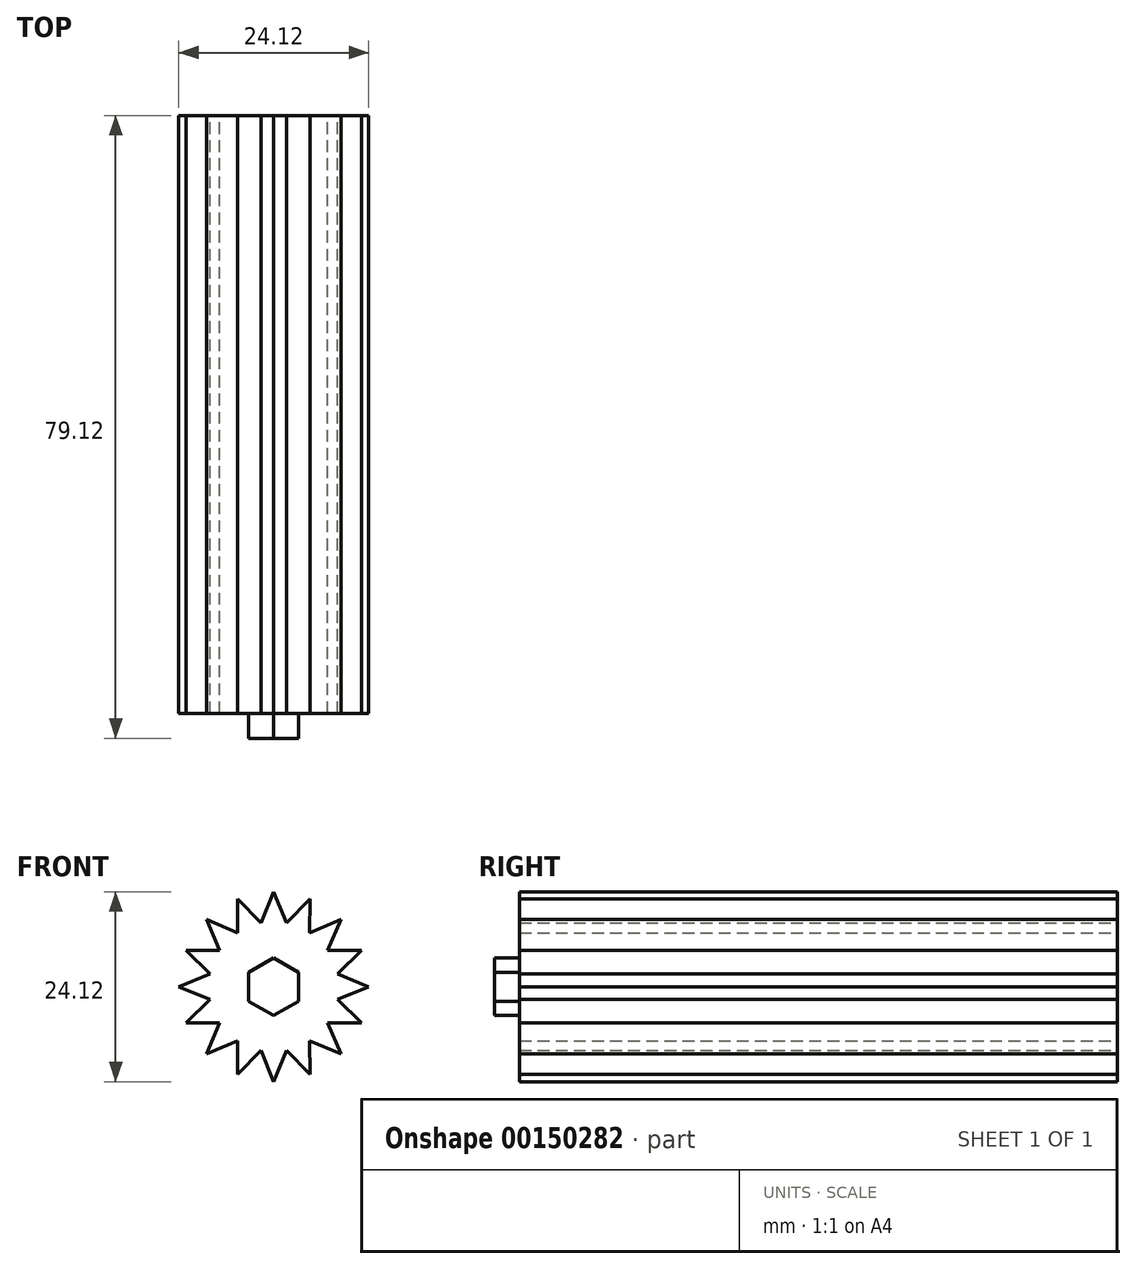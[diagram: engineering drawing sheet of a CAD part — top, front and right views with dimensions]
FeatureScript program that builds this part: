
annotation { "Feature Type Name" : "Feature", "Feature Type Description" : "" }
export const myFeature = defineFeature(function(context is Context, id is Id, definition is map)
    precondition{}
    {
        {
            var Q0;
            Q0=qCreatedBy(makeId("Front.planeOp"),FACE);
            var sketch = newSketch(context, id + "F0", { "sketchPlane" : qUnion([Q0])});
            skCircle(sketch, "E0", {"center": v(0, 0) * mm, "radius": 12.07 * mm});
            skCircle(sketch, "E1", {"center": v(0, 0) * mm, "radius": 8.26 * mm});
            skLineSegment(sketch, "E2", {"start": v(0, 12.07) * mm, "end": v(0, -12.06) * mm});
            skLineSegment(sketch, "E3", {"start": v(-4.62, 11.15) * mm, "end": v(0, 0) * mm});
            skLineSegment(sketch, "E4", {"start": v(-12.06, 0) * mm, "end": v(12.07, 0) * mm});
            skLineSegment(sketch, "E5", {"start": v(-8.53, 8.53) * mm, "end": v(0, 0) * mm});
            skLineSegment(sketch, "E6", {"start": v(-11.15, 4.62) * mm, "end": v(0, 0) * mm});
            skLineSegment(sketch, "E7", {"start": v(-11.15, -4.62) * mm, "end": v(0, 0) * mm});
            skLineSegment(sketch, "E8", {"start": v(4.62, 11.15) * mm, "end": v(0, 0) * mm});
            skLineSegment(sketch, "E9", {"start": v(8.53, 8.53) * mm, "end": v(0, 0) * mm});
            skLineSegment(sketch, "E10", {"start": v(11.15, 4.62) * mm, "end": v(0, 0) * mm});
            skLineSegment(sketch, "E11", {"start": v(11.15, -4.62) * mm, "end": v(0, 0) * mm});
            skLineSegment(sketch, "E12", {"start": v(8.53, -8.53) * mm, "end": v(0, 0) * mm});
            skLineSegment(sketch, "E13", {"start": v(-8.53, -8.53) * mm, "end": v(0, 0) * mm});
            skLineSegment(sketch, "E14", {"start": v(-4.62, -11.15) * mm, "end": v(0, 0) * mm});
            skLineSegment(sketch, "E15", {"start": v(4.62, -11.15) * mm, "end": v(0, 0) * mm});
            skLineSegment(sketch, "E16", {"start": v(-3.72, 18.68) * mm, "end": v(0, 0) * mm});
            skLineSegment(sketch, "E17", {"start": v(3.72, -18.68) * mm, "end": v(0, 0) * mm});
            skLineSegment(sketch, "E18", {"start": v(3.72, 18.68) * mm, "end": v(0, 0) * mm});
            skLineSegment(sketch, "E19", {"start": v(-3.72, -18.68) * mm, "end": v(0, 0) * mm});
            skLineSegment(sketch, "E20", {"start": v(15.84, -10.58) * mm, "end": v(0, 0) * mm});
            skLineSegment(sketch, "E21", {"start": v(18.68, -3.72) * mm, "end": v(0, 0) * mm});
            skLineSegment(sketch, "E22", {"start": v(-10.58, -15.84) * mm, "end": v(0, 0) * mm});
            skLineSegment(sketch, "E23", {"start": v(-15.84, -10.58) * mm, "end": v(0, 0) * mm});
            skLineSegment(sketch, "E24", {"start": v(-18.68, -3.72) * mm, "end": v(0, 0) * mm});
            skLineSegment(sketch, "E25", {"start": v(-18.68, 3.72) * mm, "end": v(0, 0) * mm});
            skLineSegment(sketch, "E26", {"start": v(-10.58, 15.84) * mm, "end": v(0, 0) * mm});
            skLineSegment(sketch, "E27", {"start": v(10.58, 15.84) * mm, "end": v(0, 0) * mm});
            skLineSegment(sketch, "E28", {"start": v(-15.84, 10.58) * mm, "end": v(0, 0) * mm});
            skLineSegment(sketch, "E29", {"start": v(15.84, 10.58) * mm, "end": v(0, 0) * mm});
            skLineSegment(sketch, "E30", {"start": v(18.68, 3.72) * mm, "end": v(0, 0) * mm});
            skLineSegment(sketch, "E31", {"start": v(10.58, -15.84) * mm, "end": v(0, 0) * mm});
            skLineSegment(sketch, "E32", {"start": v(-8.53, 8.53) * mm, "end": v(-4.59, 6.86) * mm});
            skLineSegment(sketch, "E33", {"start": v(-4.59, 6.86) * mm, "end": v(-4.62, 11.15) * mm});
            skLineSegment(sketch, "E34", {"start": v(-4.62, 11.15) * mm, "end": v(-1.61, 8.1) * mm});
            skLineSegment(sketch, "E35", {"start": v(-1.61, 8.1) * mm, "end": v(0, 12.07) * mm});
            skLineSegment(sketch, "E36", {"start": v(0, 12.07) * mm, "end": v(1.61, 8.1) * mm});
            skLineSegment(sketch, "E37", {"start": v(1.61, 8.1) * mm, "end": v(4.62, 11.15) * mm});
            skLineSegment(sketch, "E38", {"start": v(4.62, 11.15) * mm, "end": v(4.59, 6.86) * mm});
            skLineSegment(sketch, "E39", {"start": v(4.59, 6.86) * mm, "end": v(8.53, 8.53) * mm});
            skLineSegment(sketch, "E40", {"start": v(-8.53, 8.53) * mm, "end": v(-6.86, 4.59) * mm});
            skLineSegment(sketch, "E41", {"start": v(-6.86, 4.59) * mm, "end": v(-11.15, 4.62) * mm});
            skLineSegment(sketch, "E42", {"start": v(-11.15, 4.62) * mm, "end": v(-8.1, 1.61) * mm});
            skLineSegment(sketch, "E43", {"start": v(-8.1, 1.61) * mm, "end": v(-12.06, 0) * mm});
            skLineSegment(sketch, "E44", {"start": v(8.53, 8.53) * mm, "end": v(6.86, 4.59) * mm});
            skLineSegment(sketch, "E45", {"start": v(6.86, 4.59) * mm, "end": v(11.15, 4.62) * mm});
            skLineSegment(sketch, "E46", {"start": v(11.15, 4.62) * mm, "end": v(8.1, 1.61) * mm});
            skLineSegment(sketch, "E47", {"start": v(8.1, 1.61) * mm, "end": v(12.07, 0) * mm});
            skLineSegment(sketch, "E48", {"start": v(0, -12.06) * mm, "end": v(1.61, -8.1) * mm});
            skLineSegment(sketch, "E49", {"start": v(1.61, -8.1) * mm, "end": v(4.62, -11.15) * mm});
            skLineSegment(sketch, "E50", {"start": v(0, -12.06) * mm, "end": v(-1.61, -8.1) * mm});
            skLineSegment(sketch, "E51", {"start": v(-1.61, -8.1) * mm, "end": v(-4.62, -11.15) * mm});
            skLineSegment(sketch, "E52", {"start": v(12.07, 0) * mm, "end": v(8.1, -1.61) * mm});
            skLineSegment(sketch, "E53", {"start": v(8.1, -1.61) * mm, "end": v(11.15, -4.62) * mm});
            skLineSegment(sketch, "E54", {"start": v(-12.06, 0) * mm, "end": v(-8.1, -1.61) * mm});
            skLineSegment(sketch, "E55", {"start": v(-8.1, -1.61) * mm, "end": v(-11.15, -4.62) * mm});
            skLineSegment(sketch, "E56", {"start": v(-6.86, -4.59) * mm, "end": v(-11.15, -4.62) * mm});
            skLineSegment(sketch, "E57", {"start": v(-6.86, -4.59) * mm, "end": v(-8.53, -8.53) * mm});
            skLineSegment(sketch, "E58", {"start": v(6.86, -4.59) * mm, "end": v(11.15, -4.62) * mm});
            skLineSegment(sketch, "E59", {"start": v(6.86, -4.59) * mm, "end": v(8.53, -8.53) * mm});
            skLineSegment(sketch, "E60", {"start": v(4.59, -6.86) * mm, "end": v(8.53, -8.53) * mm});
            skLineSegment(sketch, "E61", {"start": v(-4.59, -6.86) * mm, "end": v(-8.53, -8.53) * mm});
            skLineSegment(sketch, "E62", {"start": v(-4.59, -6.86) * mm, "end": v(-4.62, -11.15) * mm});
            skLineSegment(sketch, "E63", {"start": v(4.59, -6.86) * mm, "end": v(4.62, -11.15) * mm});
            skSolve(sketch);
        }
        {
            var Q0;
            {var subQ0=sQuery(id+"F0.wireOp",EDGE,"E47");Q0=makeQuery(id+"F0.imprint","IMPRINT",FACE,{"disambiguationData":[TD([[makeQuery(id+"F0.imprint","IMPRINT",EDGE,{"derivedFrom":subQ0}),-1.0]])]});}
            var Q1;
            {var subQ0=sQuery(id+"F0.wireOp",EDGE,"E46");Q1=makeQuery(id+"F0.imprint","IMPRINT",FACE,{"disambiguationData":[TD([[makeQuery(id+"F0.imprint","IMPRINT",EDGE,{"derivedFrom":subQ0}),-1.0]])]});}
            var Q2;
            {var subQ0=sQuery(id+"F0.wireOp",EDGE,"E45");Q2=makeQuery(id+"F0.imprint","IMPRINT",FACE,{"disambiguationData":[TD([[makeQuery(id+"F0.imprint","IMPRINT",EDGE,{"derivedFrom":subQ0}),-1.0]])]});}
            var Q3;
            {var subQ0=sQuery(id+"F0.wireOp",EDGE,"E44");Q3=makeQuery(id+"F0.imprint","IMPRINT",FACE,{"disambiguationData":[TD([[makeQuery(id+"F0.imprint","IMPRINT",EDGE,{"derivedFrom":subQ0}),-1.0]])]});}
            var Q4;
            {var subQ0=sQuery(id+"F0.wireOp",EDGE,"E39");Q4=makeQuery(id+"F0.imprint","IMPRINT",FACE,{"disambiguationData":[TD([[makeQuery(id+"F0.imprint","IMPRINT",EDGE,{"derivedFrom":subQ0}),-1.0]])]});}
            var Q5;
            {var subQ0=sQuery(id+"F0.wireOp",EDGE,"E38");Q5=makeQuery(id+"F0.imprint","IMPRINT",FACE,{"disambiguationData":[TD([[makeQuery(id+"F0.imprint","IMPRINT",EDGE,{"derivedFrom":subQ0}),-1.0]])]});}
            var Q6;
            {var subQ0=sQuery(id+"F0.wireOp",EDGE,"E37");Q6=makeQuery(id+"F0.imprint","IMPRINT",FACE,{"disambiguationData":[TD([[makeQuery(id+"F0.imprint","IMPRINT",EDGE,{"derivedFrom":subQ0}),-1.0]])]});}
            var Q7;
            {var subQ0=sQuery(id+"F0.wireOp",EDGE,"E36");Q7=makeQuery(id+"F0.imprint","IMPRINT",FACE,{"disambiguationData":[TD([[makeQuery(id+"F0.imprint","IMPRINT",EDGE,{"derivedFrom":subQ0}),-1.0]])]});}
            var Q8;
            {var subQ0=sQuery(id+"F0.wireOp",EDGE,"E35");Q8=makeQuery(id+"F0.imprint","IMPRINT",FACE,{"disambiguationData":[TD([[makeQuery(id+"F0.imprint","IMPRINT",EDGE,{"derivedFrom":subQ0}),-1.0]])]});}
            var Q9;
            {var subQ0=sQuery(id+"F0.wireOp",EDGE,"E34");Q9=makeQuery(id+"F0.imprint","IMPRINT",FACE,{"disambiguationData":[TD([[makeQuery(id+"F0.imprint","IMPRINT",EDGE,{"derivedFrom":subQ0}),-1.0]])]});}
            var Q10;
            {var subQ0=sQuery(id+"F0.wireOp",EDGE,"E33");Q10=makeQuery(id+"F0.imprint","IMPRINT",FACE,{"disambiguationData":[TD([[makeQuery(id+"F0.imprint","IMPRINT",EDGE,{"derivedFrom":subQ0}),-1.0]])]});}
            var Q11;
            {var subQ0=sQuery(id+"F0.wireOp",EDGE,"E32");Q11=makeQuery(id+"F0.imprint","IMPRINT",FACE,{"disambiguationData":[TD([[makeQuery(id+"F0.imprint","IMPRINT",EDGE,{"derivedFrom":subQ0}),-1.0]])]});}
            var Q12;
            {var subQ0=sQuery(id+"F0.wireOp",EDGE,"E40");Q12=makeQuery(id+"F0.imprint","IMPRINT",FACE,{"disambiguationData":[TD([[makeQuery(id+"F0.imprint","IMPRINT",EDGE,{"derivedFrom":subQ0}),1.0]])]});}
            var Q13;
            {var subQ0=sQuery(id+"F0.wireOp",EDGE,"E41");Q13=makeQuery(id+"F0.imprint","IMPRINT",FACE,{"disambiguationData":[TD([[makeQuery(id+"F0.imprint","IMPRINT",EDGE,{"derivedFrom":subQ0}),1.0]])]});}
            var Q14;
            {var subQ0=sQuery(id+"F0.wireOp",EDGE,"E42");Q14=makeQuery(id+"F0.imprint","IMPRINT",FACE,{"disambiguationData":[TD([[makeQuery(id+"F0.imprint","IMPRINT",EDGE,{"derivedFrom":subQ0}),1.0]])]});}
            var Q15;
            {var subQ0=sQuery(id+"F0.wireOp",EDGE,"E43");Q15=makeQuery(id+"F0.imprint","IMPRINT",FACE,{"disambiguationData":[TD([[makeQuery(id+"F0.imprint","IMPRINT",EDGE,{"derivedFrom":subQ0}),1.0]])]});}
            var Q16;
            {var subQ0=sQuery(id+"F0.wireOp",EDGE,"E54");Q16=makeQuery(id+"F0.imprint","IMPRINT",FACE,{"disambiguationData":[TD([[makeQuery(id+"F0.imprint","IMPRINT",EDGE,{"derivedFrom":subQ0}),1.0]])]});}
            var Q17;
            {var subQ0=sQuery(id+"F0.wireOp",EDGE,"E55");Q17=makeQuery(id+"F0.imprint","IMPRINT",FACE,{"disambiguationData":[TD([[makeQuery(id+"F0.imprint","IMPRINT",EDGE,{"derivedFrom":subQ0}),1.0]])]});}
            var Q18;
            {var subQ0=sQuery(id+"F0.wireOp",EDGE,"E56");Q18=makeQuery(id+"F0.imprint","IMPRINT",FACE,{"disambiguationData":[TD([[makeQuery(id+"F0.imprint","IMPRINT",EDGE,{"derivedFrom":subQ0}),-1.0]])]});}
            var Q19;
            {var subQ0=sQuery(id+"F0.wireOp",EDGE,"E57");Q19=makeQuery(id+"F0.imprint","IMPRINT",FACE,{"disambiguationData":[TD([[makeQuery(id+"F0.imprint","IMPRINT",EDGE,{"derivedFrom":subQ0}),1.0]])]});}
            var Q20;
            {var subQ0=sQuery(id+"F0.wireOp",EDGE,"E61");Q20=makeQuery(id+"F0.imprint","IMPRINT",FACE,{"disambiguationData":[TD([[makeQuery(id+"F0.imprint","IMPRINT",EDGE,{"derivedFrom":subQ0}),-1.0]])]});}
            var Q21;
            {var subQ0=sQuery(id+"F0.wireOp",EDGE,"E62");Q21=makeQuery(id+"F0.imprint","IMPRINT",FACE,{"disambiguationData":[TD([[makeQuery(id+"F0.imprint","IMPRINT",EDGE,{"derivedFrom":subQ0}),1.0]])]});}
            var Q22;
            {var subQ0=sQuery(id+"F0.wireOp",EDGE,"E51");Q22=makeQuery(id+"F0.imprint","IMPRINT",FACE,{"disambiguationData":[TD([[makeQuery(id+"F0.imprint","IMPRINT",EDGE,{"derivedFrom":subQ0}),-1.0]])]});}
            var Q23;
            {var subQ0=sQuery(id+"F0.wireOp",EDGE,"E50");Q23=makeQuery(id+"F0.imprint","IMPRINT",FACE,{"disambiguationData":[TD([[makeQuery(id+"F0.imprint","IMPRINT",EDGE,{"derivedFrom":subQ0}),-1.0]])]});}
            var Q24;
            {var subQ0=sQuery(id+"F0.wireOp",EDGE,"E48");Q24=makeQuery(id+"F0.imprint","IMPRINT",FACE,{"disambiguationData":[TD([[makeQuery(id+"F0.imprint","IMPRINT",EDGE,{"derivedFrom":subQ0}),1.0]])]});}
            var Q25;
            {var subQ0=sQuery(id+"F0.wireOp",EDGE,"E49");Q25=makeQuery(id+"F0.imprint","IMPRINT",FACE,{"disambiguationData":[TD([[makeQuery(id+"F0.imprint","IMPRINT",EDGE,{"derivedFrom":subQ0}),1.0]])]});}
            var Q26;
            {var subQ0=sQuery(id+"F0.wireOp",EDGE,"E63");Q26=makeQuery(id+"F0.imprint","IMPRINT",FACE,{"disambiguationData":[TD([[makeQuery(id+"F0.imprint","IMPRINT",EDGE,{"derivedFrom":subQ0}),-1.0]])]});}
            var Q27;
            {var subQ0=sQuery(id+"F0.wireOp",EDGE,"E60");Q27=makeQuery(id+"F0.imprint","IMPRINT",FACE,{"disambiguationData":[TD([[makeQuery(id+"F0.imprint","IMPRINT",EDGE,{"derivedFrom":subQ0}),1.0]])]});}
            var Q28;
            {var subQ0=sQuery(id+"F0.wireOp",EDGE,"E59");Q28=makeQuery(id+"F0.imprint","IMPRINT",FACE,{"disambiguationData":[TD([[makeQuery(id+"F0.imprint","IMPRINT",EDGE,{"derivedFrom":subQ0}),-1.0]])]});}
            var Q29;
            {var subQ0=sQuery(id+"F0.wireOp",EDGE,"E58");Q29=makeQuery(id+"F0.imprint","IMPRINT",FACE,{"disambiguationData":[TD([[makeQuery(id+"F0.imprint","IMPRINT",EDGE,{"derivedFrom":subQ0}),1.0]])]});}
            var Q30;
            {var subQ0=sQuery(id+"F0.wireOp",EDGE,"E53");Q30=makeQuery(id+"F0.imprint","IMPRINT",FACE,{"disambiguationData":[TD([[makeQuery(id+"F0.imprint","IMPRINT",EDGE,{"derivedFrom":subQ0}),-1.0]])]});}
            var Q31;
            {var subQ0=sQuery(id+"F0.wireOp",EDGE,"E52");Q31=makeQuery(id+"F0.imprint","IMPRINT",FACE,{"disambiguationData":[TD([[makeQuery(id+"F0.imprint","IMPRINT",EDGE,{"derivedFrom":subQ0}),-1.0]])]});}
            var Q32;
            {var subQ1=sQuery(id+"F0.wireOp",EDGE,"E1");var subQ3=sQuery(id+"F0.wireOp",EDGE,"E3");var subQ4=makeQuery(id+"F0.imprint","INTERSECT",VERTEX,{"derivedFrom":[subQ1,subQ3]});Q32=makeQuery(id+"F0.imprint","IMPRINT",FACE,{"disambiguationData":[TD([[makeQuery(id+"F0.imprint","IMPRINT",EDGE,{"disambiguationData":[TD([[subQ4,1.0]])],"derivedFrom":subQ1}),1.0]])]});}
            var Q33;
            {var subQ1=sQuery(id+"F0.wireOp",EDGE,"E1");var subQ3=sQuery(id+"F0.wireOp",EDGE,"E3");var subQ4=makeQuery(id+"F0.imprint","INTERSECT",VERTEX,{"derivedFrom":[subQ1,subQ3]});Q33=makeQuery(id+"F0.imprint","IMPRINT",FACE,{"disambiguationData":[TD([[makeQuery(id+"F0.imprint","IMPRINT",EDGE,{"disambiguationData":[TD([[subQ4,-1.0]])],"derivedFrom":subQ1}),1.0]])]});}
            var Q34;
            {var subQ1=sQuery(id+"F0.wireOp",EDGE,"E1");var subQ3=sQuery(id+"F0.wireOp",EDGE,"E2");var subQ4=makeQuery(id+"F0.imprint","INTERSECT",VERTEX,{"disambiguationData":[OD(0.0)],"derivedFrom":[subQ1,subQ3]});Q34=makeQuery(id+"F0.imprint","IMPRINT",FACE,{"disambiguationData":[TD([[makeQuery(id+"F0.imprint","IMPRINT",EDGE,{"disambiguationData":[TD([[subQ4,-1.0]])],"derivedFrom":subQ1}),1.0]])]});}
            var Q35;
            {var subQ1=sQuery(id+"F0.wireOp",EDGE,"E1");var subQ3=sQuery(id+"F0.wireOp",EDGE,"E2");var subQ4=makeQuery(id+"F0.imprint","INTERSECT",VERTEX,{"disambiguationData":[OD(0.0)],"derivedFrom":[subQ1,subQ3]});Q35=makeQuery(id+"F0.imprint","IMPRINT",FACE,{"disambiguationData":[TD([[makeQuery(id+"F0.imprint","IMPRINT",EDGE,{"disambiguationData":[TD([[subQ4,1.0]])],"derivedFrom":subQ1}),1.0]])]});}
            var Q36;
            {var subQ1=sQuery(id+"F0.wireOp",EDGE,"E1");var subQ3=sQuery(id+"F0.wireOp",EDGE,"E8");var subQ4=makeQuery(id+"F0.imprint","INTERSECT",VERTEX,{"derivedFrom":[subQ1,subQ3]});Q36=makeQuery(id+"F0.imprint","IMPRINT",FACE,{"disambiguationData":[TD([[makeQuery(id+"F0.imprint","IMPRINT",EDGE,{"disambiguationData":[TD([[subQ4,-1.0]])],"derivedFrom":subQ1}),1.0]])]});}
            var Q37;
            {var subQ1=sQuery(id+"F0.wireOp",EDGE,"E1");var subQ3=sQuery(id+"F0.wireOp",EDGE,"E8");var subQ4=makeQuery(id+"F0.imprint","INTERSECT",VERTEX,{"derivedFrom":[subQ1,subQ3]});Q37=makeQuery(id+"F0.imprint","IMPRINT",FACE,{"disambiguationData":[TD([[makeQuery(id+"F0.imprint","IMPRINT",EDGE,{"disambiguationData":[TD([[subQ4,1.0]])],"derivedFrom":subQ1}),1.0]])]});}
            var Q38;
            {var subQ1=sQuery(id+"F0.wireOp",EDGE,"E1");var subQ3=sQuery(id+"F0.wireOp",EDGE,"E9");var subQ4=makeQuery(id+"F0.imprint","INTERSECT",VERTEX,{"derivedFrom":[subQ1,subQ3]});Q38=makeQuery(id+"F0.imprint","IMPRINT",FACE,{"disambiguationData":[TD([[makeQuery(id+"F0.imprint","IMPRINT",EDGE,{"disambiguationData":[TD([[subQ4,-1.0]])],"derivedFrom":subQ1}),1.0]])]});}
            var Q39;
            {var subQ1=sQuery(id+"F0.wireOp",EDGE,"E1");var subQ3=sQuery(id+"F0.wireOp",EDGE,"E9");var subQ4=makeQuery(id+"F0.imprint","INTERSECT",VERTEX,{"derivedFrom":[subQ1,subQ3]});Q39=makeQuery(id+"F0.imprint","IMPRINT",FACE,{"disambiguationData":[TD([[makeQuery(id+"F0.imprint","IMPRINT",EDGE,{"disambiguationData":[TD([[subQ4,1.0]])],"derivedFrom":subQ1}),1.0]])]});}
            var Q40;
            {var subQ1=sQuery(id+"F0.wireOp",EDGE,"E1");var subQ3=sQuery(id+"F0.wireOp",EDGE,"E10");var subQ4=makeQuery(id+"F0.imprint","INTERSECT",VERTEX,{"derivedFrom":[subQ1,subQ3]});Q40=makeQuery(id+"F0.imprint","IMPRINT",FACE,{"disambiguationData":[TD([[makeQuery(id+"F0.imprint","IMPRINT",EDGE,{"disambiguationData":[TD([[subQ4,-1.0]])],"derivedFrom":subQ1}),1.0]])]});}
            var Q41;
            {var subQ1=sQuery(id+"F0.wireOp",EDGE,"E1");var subQ3=sQuery(id+"F0.wireOp",EDGE,"E10");var subQ4=makeQuery(id+"F0.imprint","INTERSECT",VERTEX,{"derivedFrom":[subQ1,subQ3]});Q41=makeQuery(id+"F0.imprint","IMPRINT",FACE,{"disambiguationData":[TD([[makeQuery(id+"F0.imprint","IMPRINT",EDGE,{"disambiguationData":[TD([[subQ4,1.0]])],"derivedFrom":subQ1}),1.0]])]});}
            var Q42;
            {var subQ1=sQuery(id+"F0.wireOp",EDGE,"E1");var subQ3=sQuery(id+"F0.wireOp",EDGE,"E4");var subQ4=makeQuery(id+"F0.imprint","INTERSECT",VERTEX,{"disambiguationData":[OD(0.0)],"derivedFrom":[subQ1,subQ3]});Q42=makeQuery(id+"F0.imprint","IMPRINT",FACE,{"disambiguationData":[TD([[makeQuery(id+"F0.imprint","IMPRINT",EDGE,{"disambiguationData":[TD([[subQ4,-1.0]])],"derivedFrom":subQ1}),1.0]])]});}
            var Q43;
            {var subQ1=sQuery(id+"F0.wireOp",EDGE,"E1");var subQ3=sQuery(id+"F0.wireOp",EDGE,"E4");var subQ4=makeQuery(id+"F0.imprint","INTERSECT",VERTEX,{"disambiguationData":[OD(0.0)],"derivedFrom":[subQ1,subQ3]});Q43=makeQuery(id+"F0.imprint","IMPRINT",FACE,{"disambiguationData":[TD([[makeQuery(id+"F0.imprint","IMPRINT",EDGE,{"disambiguationData":[TD([[subQ4,1.0]])],"derivedFrom":subQ1}),1.0]])]});}
            var Q44;
            {var subQ1=sQuery(id+"F0.wireOp",EDGE,"E1");var subQ3=sQuery(id+"F0.wireOp",EDGE,"E11");var subQ4=makeQuery(id+"F0.imprint","INTERSECT",VERTEX,{"derivedFrom":[subQ1,subQ3]});Q44=makeQuery(id+"F0.imprint","IMPRINT",FACE,{"disambiguationData":[TD([[makeQuery(id+"F0.imprint","IMPRINT",EDGE,{"disambiguationData":[TD([[subQ4,-1.0]])],"derivedFrom":subQ1}),1.0]])]});}
            var Q45;
            {var subQ1=sQuery(id+"F0.wireOp",EDGE,"E1");var subQ3=sQuery(id+"F0.wireOp",EDGE,"E11");var subQ4=makeQuery(id+"F0.imprint","INTERSECT",VERTEX,{"derivedFrom":[subQ1,subQ3]});Q45=makeQuery(id+"F0.imprint","IMPRINT",FACE,{"disambiguationData":[TD([[makeQuery(id+"F0.imprint","IMPRINT",EDGE,{"disambiguationData":[TD([[subQ4,1.0]])],"derivedFrom":subQ1}),1.0]])]});}
            var Q46;
            {var subQ1=sQuery(id+"F0.wireOp",EDGE,"E1");var subQ3=sQuery(id+"F0.wireOp",EDGE,"E12");var subQ4=makeQuery(id+"F0.imprint","INTERSECT",VERTEX,{"derivedFrom":[subQ1,subQ3]});Q46=makeQuery(id+"F0.imprint","IMPRINT",FACE,{"disambiguationData":[TD([[makeQuery(id+"F0.imprint","IMPRINT",EDGE,{"disambiguationData":[TD([[subQ4,-1.0]])],"derivedFrom":subQ1}),1.0]])]});}
            var Q47;
            {var subQ1=sQuery(id+"F0.wireOp",EDGE,"E1");var subQ3=sQuery(id+"F0.wireOp",EDGE,"E12");var subQ4=makeQuery(id+"F0.imprint","INTERSECT",VERTEX,{"derivedFrom":[subQ1,subQ3]});Q47=makeQuery(id+"F0.imprint","IMPRINT",FACE,{"disambiguationData":[TD([[makeQuery(id+"F0.imprint","IMPRINT",EDGE,{"disambiguationData":[TD([[subQ4,1.0]])],"derivedFrom":subQ1}),1.0]])]});}
            var Q48;
            {var subQ1=sQuery(id+"F0.wireOp",EDGE,"E1");var subQ3=sQuery(id+"F0.wireOp",EDGE,"E15");var subQ4=makeQuery(id+"F0.imprint","INTERSECT",VERTEX,{"derivedFrom":[subQ1,subQ3]});Q48=makeQuery(id+"F0.imprint","IMPRINT",FACE,{"disambiguationData":[TD([[makeQuery(id+"F0.imprint","IMPRINT",EDGE,{"disambiguationData":[TD([[subQ4,-1.0]])],"derivedFrom":subQ1}),1.0]])]});}
            var Q49;
            {var subQ1=sQuery(id+"F0.wireOp",EDGE,"E1");var subQ3=sQuery(id+"F0.wireOp",EDGE,"E14");var subQ4=makeQuery(id+"F0.imprint","INTERSECT",VERTEX,{"derivedFrom":[subQ1,subQ3]});Q49=makeQuery(id+"F0.imprint","IMPRINT",FACE,{"disambiguationData":[TD([[makeQuery(id+"F0.imprint","IMPRINT",EDGE,{"disambiguationData":[TD([[subQ4,-1.0]])],"derivedFrom":subQ1}),1.0]])]});}
            var Q50;
            {var subQ1=sQuery(id+"F0.wireOp",EDGE,"E1");var subQ3=sQuery(id+"F0.wireOp",EDGE,"E14");var subQ4=makeQuery(id+"F0.imprint","INTERSECT",VERTEX,{"derivedFrom":[subQ1,subQ3]});Q50=makeQuery(id+"F0.imprint","IMPRINT",FACE,{"disambiguationData":[TD([[makeQuery(id+"F0.imprint","IMPRINT",EDGE,{"disambiguationData":[TD([[subQ4,1.0]])],"derivedFrom":subQ1}),1.0]])]});}
            var Q51;
            {var subQ1=sQuery(id+"F0.wireOp",EDGE,"E1");var subQ3=sQuery(id+"F0.wireOp",EDGE,"E13");var subQ4=makeQuery(id+"F0.imprint","INTERSECT",VERTEX,{"derivedFrom":[subQ1,subQ3]});Q51=makeQuery(id+"F0.imprint","IMPRINT",FACE,{"disambiguationData":[TD([[makeQuery(id+"F0.imprint","IMPRINT",EDGE,{"disambiguationData":[TD([[subQ4,-1.0]])],"derivedFrom":subQ1}),1.0]])]});}
            var Q52;
            {var subQ1=sQuery(id+"F0.wireOp",EDGE,"E1");var subQ3=sQuery(id+"F0.wireOp",EDGE,"E13");var subQ4=makeQuery(id+"F0.imprint","INTERSECT",VERTEX,{"derivedFrom":[subQ1,subQ3]});Q52=makeQuery(id+"F0.imprint","IMPRINT",FACE,{"disambiguationData":[TD([[makeQuery(id+"F0.imprint","IMPRINT",EDGE,{"disambiguationData":[TD([[subQ4,1.0]])],"derivedFrom":subQ1}),1.0]])]});}
            var Q53;
            {var subQ1=sQuery(id+"F0.wireOp",EDGE,"E1");var subQ3=sQuery(id+"F0.wireOp",EDGE,"E7");var subQ4=makeQuery(id+"F0.imprint","INTERSECT",VERTEX,{"derivedFrom":[subQ1,subQ3]});Q53=makeQuery(id+"F0.imprint","IMPRINT",FACE,{"disambiguationData":[TD([[makeQuery(id+"F0.imprint","IMPRINT",EDGE,{"disambiguationData":[TD([[subQ4,-1.0]])],"derivedFrom":subQ1}),1.0]])]});}
            var Q54;
            {var subQ1=sQuery(id+"F0.wireOp",EDGE,"E1");var subQ3=sQuery(id+"F0.wireOp",EDGE,"E7");var subQ4=makeQuery(id+"F0.imprint","INTERSECT",VERTEX,{"derivedFrom":[subQ1,subQ3]});Q54=makeQuery(id+"F0.imprint","IMPRINT",FACE,{"disambiguationData":[TD([[makeQuery(id+"F0.imprint","IMPRINT",EDGE,{"disambiguationData":[TD([[subQ4,1.0]])],"derivedFrom":subQ1}),1.0]])]});}
            var Q55;
            {var subQ1=sQuery(id+"F0.wireOp",EDGE,"E1");var subQ3=sQuery(id+"F0.wireOp",EDGE,"E4");var subQ4=makeQuery(id+"F0.imprint","INTERSECT",VERTEX,{"disambiguationData":[OD(1.0)],"derivedFrom":[subQ1,subQ3]});Q55=makeQuery(id+"F0.imprint","IMPRINT",FACE,{"disambiguationData":[TD([[makeQuery(id+"F0.imprint","IMPRINT",EDGE,{"disambiguationData":[TD([[subQ4,-1.0]])],"derivedFrom":subQ1}),1.0]])]});}
            var Q56;
            {var subQ1=sQuery(id+"F0.wireOp",EDGE,"E1");var subQ3=sQuery(id+"F0.wireOp",EDGE,"E4");var subQ4=makeQuery(id+"F0.imprint","INTERSECT",VERTEX,{"disambiguationData":[OD(1.0)],"derivedFrom":[subQ1,subQ3]});Q56=makeQuery(id+"F0.imprint","IMPRINT",FACE,{"disambiguationData":[TD([[makeQuery(id+"F0.imprint","IMPRINT",EDGE,{"disambiguationData":[TD([[subQ4,1.0]])],"derivedFrom":subQ1}),1.0]])]});}
            var Q57;
            {var subQ1=sQuery(id+"F0.wireOp",EDGE,"E1");var subQ3=sQuery(id+"F0.wireOp",EDGE,"E6");var subQ4=makeQuery(id+"F0.imprint","INTERSECT",VERTEX,{"derivedFrom":[subQ1,subQ3]});Q57=makeQuery(id+"F0.imprint","IMPRINT",FACE,{"disambiguationData":[TD([[makeQuery(id+"F0.imprint","IMPRINT",EDGE,{"disambiguationData":[TD([[subQ4,-1.0]])],"derivedFrom":subQ1}),1.0]])]});}
            var Q58;
            {var subQ1=sQuery(id+"F0.wireOp",EDGE,"E1");var subQ3=sQuery(id+"F0.wireOp",EDGE,"E6");var subQ4=makeQuery(id+"F0.imprint","INTERSECT",VERTEX,{"derivedFrom":[subQ1,subQ3]});Q58=makeQuery(id+"F0.imprint","IMPRINT",FACE,{"disambiguationData":[TD([[makeQuery(id+"F0.imprint","IMPRINT",EDGE,{"disambiguationData":[TD([[subQ4,1.0]])],"derivedFrom":subQ1}),1.0]])]});}
            var Q59;
            {var subQ1=sQuery(id+"F0.wireOp",EDGE,"E1");var subQ3=sQuery(id+"F0.wireOp",EDGE,"E5");var subQ4=makeQuery(id+"F0.imprint","INTERSECT",VERTEX,{"derivedFrom":[subQ1,subQ3]});Q59=makeQuery(id+"F0.imprint","IMPRINT",FACE,{"disambiguationData":[TD([[makeQuery(id+"F0.imprint","IMPRINT",EDGE,{"disambiguationData":[TD([[subQ4,-1.0]])],"derivedFrom":subQ1}),1.0]])]});}
            var Q60;
            {var subQ1=sQuery(id+"F0.wireOp",EDGE,"E1");var subQ3=sQuery(id+"F0.wireOp",EDGE,"E5");var subQ4=makeQuery(id+"F0.imprint","INTERSECT",VERTEX,{"derivedFrom":[subQ1,subQ3]});Q60=makeQuery(id+"F0.imprint","IMPRINT",FACE,{"disambiguationData":[TD([[makeQuery(id+"F0.imprint","IMPRINT",EDGE,{"disambiguationData":[TD([[subQ4,1.0]])],"derivedFrom":subQ1}),1.0]])]});}
            var Q61;
            {var subQ1=sQuery(id+"F0.wireOp",EDGE,"E1");var subQ3=sQuery(id+"F0.wireOp",EDGE,"E15");var subQ4=makeQuery(id+"F0.imprint","INTERSECT",VERTEX,{"derivedFrom":[subQ1,subQ3]});Q61=makeQuery(id+"F0.imprint","IMPRINT",FACE,{"disambiguationData":[TD([[makeQuery(id+"F0.imprint","IMPRINT",EDGE,{"disambiguationData":[TD([[subQ4,1.0]])],"derivedFrom":subQ1}),1.0]])]});}
            var Q62;
            {var subQ1=sQuery(id+"F0.wireOp",EDGE,"E1");var subQ3=sQuery(id+"F0.wireOp",EDGE,"E2");var subQ4=makeQuery(id+"F0.imprint","INTERSECT",VERTEX,{"disambiguationData":[OD(1.0)],"derivedFrom":[subQ1,subQ3]});Q62=makeQuery(id+"F0.imprint","IMPRINT",FACE,{"disambiguationData":[TD([[makeQuery(id+"F0.imprint","IMPRINT",EDGE,{"disambiguationData":[TD([[subQ4,-1.0]])],"derivedFrom":subQ1}),1.0]])]});}
            var Q63;
            {var subQ1=sQuery(id+"F0.wireOp",EDGE,"E1");var subQ3=sQuery(id+"F0.wireOp",EDGE,"E2");var subQ4=makeQuery(id+"F0.imprint","INTERSECT",VERTEX,{"disambiguationData":[OD(1.0)],"derivedFrom":[subQ1,subQ3]});Q63=makeQuery(id+"F0.imprint","IMPRINT",FACE,{"disambiguationData":[TD([[makeQuery(id+"F0.imprint","IMPRINT",EDGE,{"disambiguationData":[TD([[subQ4,1.0]])],"derivedFrom":subQ1}),1.0]])]});}
            extrude(context, id + "F1", {"entities" : qUnion([Q0, Q1, Q2, Q3, Q4, Q5, Q6, Q7, Q8, Q9, Q10, Q11, Q12, Q13, Q14, Q15, Q16, Q17, Q18, Q19, Q20, Q21, Q22, Q23, Q24, Q25, Q26, Q27, Q28, Q29, Q30, Q31, Q32, Q33, Q34, Q35, Q36, Q37, Q38, Q39, Q40, Q41, Q42, Q43, Q44, Q45, Q46, Q47, Q48, Q49, Q50, Q51, Q52, Q53, Q54, Q55, Q56, Q57, Q58, Q59, Q60, Q61, Q62, Q63]), "depth" : 75.95 * mm});
        }
        {
            var Q0;
            Q0=makeQuery(id+"F1.opExtrude","CAP_FACE",FACE,{"disambiguationData":[OSD([sQuery(id+"F0.wireOp",EDGE,"E32"),sQuery(id+"F0.wireOp",EDGE,"E33"),sQuery(id+"F0.wireOp",EDGE,"E34"),sQuery(id+"F0.wireOp",EDGE,"E35"),sQuery(id+"F0.wireOp",EDGE,"E36"),sQuery(id+"F0.wireOp",EDGE,"E37"),sQuery(id+"F0.wireOp",EDGE,"E38"),sQuery(id+"F0.wireOp",EDGE,"E39"),sQuery(id+"F0.wireOp",EDGE,"E40"),sQuery(id+"F0.wireOp",EDGE,"E41"),sQuery(id+"F0.wireOp",EDGE,"E42"),sQuery(id+"F0.wireOp",EDGE,"E43"),sQuery(id+"F0.wireOp",EDGE,"E44"),sQuery(id+"F0.wireOp",EDGE,"E45"),sQuery(id+"F0.wireOp",EDGE,"E46"),sQuery(id+"F0.wireOp",EDGE,"E47"),sQuery(id+"F0.wireOp",EDGE,"E48"),sQuery(id+"F0.wireOp",EDGE,"E49"),sQuery(id+"F0.wireOp",EDGE,"E50"),sQuery(id+"F0.wireOp",EDGE,"E51"),sQuery(id+"F0.wireOp",EDGE,"E52"),sQuery(id+"F0.wireOp",EDGE,"E53"),sQuery(id+"F0.wireOp",EDGE,"E54"),sQuery(id+"F0.wireOp",EDGE,"E55"),sQuery(id+"F0.wireOp",EDGE,"E56"),sQuery(id+"F0.wireOp",EDGE,"E57"),sQuery(id+"F0.wireOp",EDGE,"E58"),sQuery(id+"F0.wireOp",EDGE,"E59"),sQuery(id+"F0.wireOp",EDGE,"E60"),sQuery(id+"F0.wireOp",EDGE,"E61"),sQuery(id+"F0.wireOp",EDGE,"E62"),sQuery(id+"F0.wireOp",EDGE,"E63")])],"isStart":false});
            var sketch = newSketch(context, id + "F2", { "sketchPlane" : qUnion([Q0])});
            skCircle(sketch, "E64.cCircle", {"center": v(0, 0) * mm, "radius": 3.18 * mm, "construction": true});
            skLineSegment(sketch, "E64.0", {"start": v(-3.18, -1.83) * mm, "end": v(-3.18, 1.83) * mm});
            skLineSegment(sketch, "E64.1", {"start": v(-3.18, 1.83) * mm, "end": v(0, 3.67) * mm});
            skLineSegment(sketch, "E64.2", {"start": v(0, 3.67) * mm, "end": v(3.18, 1.83) * mm});
            skLineSegment(sketch, "E64.3", {"start": v(3.17, 1.83) * mm, "end": v(3.18, -1.83) * mm});
            skLineSegment(sketch, "E64.4", {"start": v(3.18, -1.83) * mm, "end": v(0, -3.67) * mm});
            skLineSegment(sketch, "E64.5", {"start": v(0, -3.67) * mm, "end": v(-3.18, -1.83) * mm});
            skPoint(sketch, "E64.0.midPoint", {"position": v(-3.18, 0) * mm});
            skSolve(sketch);
        }
        {
            var Q0;
            Q0 = qSketchRegion(id + "F2", true);
            extrude(context, id + "F3", {"entities" : qUnion([Q0]), "operationType" : NewBodyOperationType.ADD, "depth" : 3.17 * mm});
        }
    });
